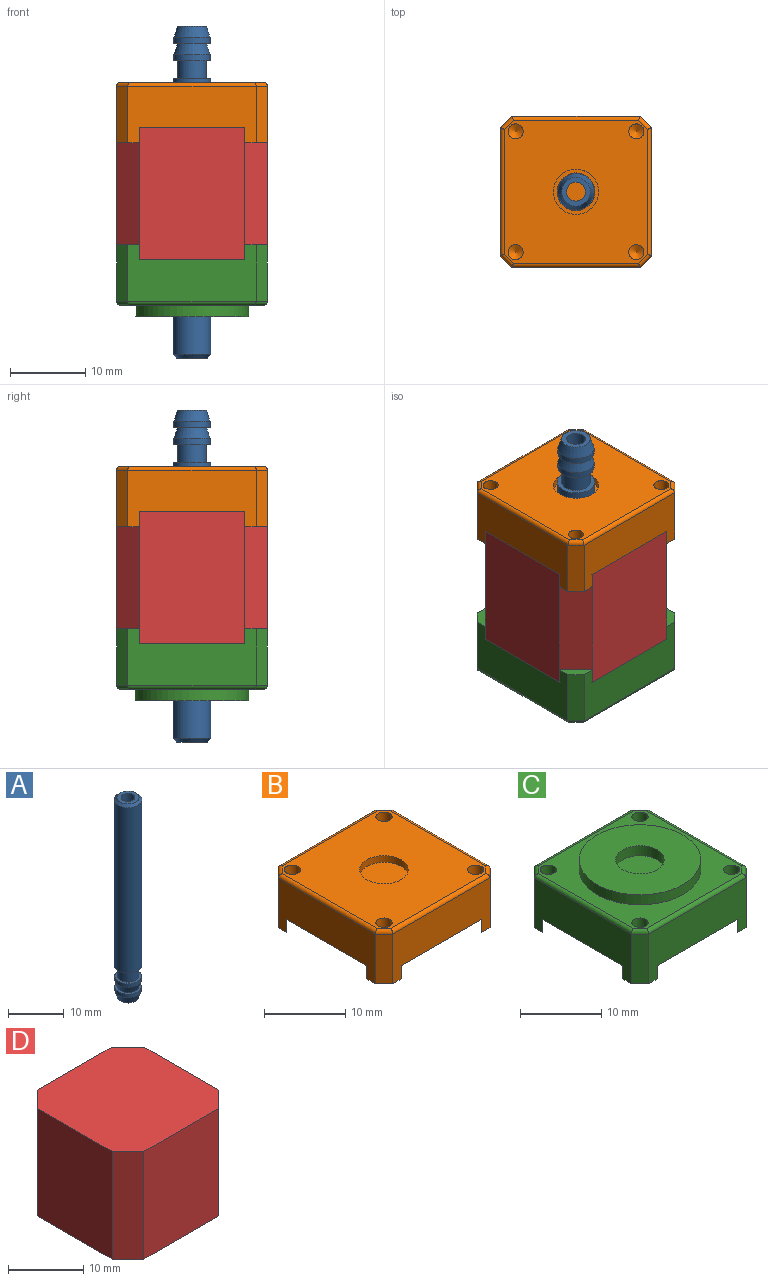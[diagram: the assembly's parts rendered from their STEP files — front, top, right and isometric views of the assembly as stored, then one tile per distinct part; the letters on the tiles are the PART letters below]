
ASSEMBLY  parts=4 mates=3
PART A: 13 faces, bbox 5x5x44 mm
  f0: plane 3.8x3.8mm, normal (0,0,-1), area 6.4mm2, adj f4,f7
  f1: cylinder r=2.5mm len=36.5mm, axis (0,0,-1), area 573.3mm2, adj f3,f6
  f2: plane 4x4mm, normal (0,0,1), area 7.7mm2, adj f3,f4
  f3: cone r=2mm half-angle=45deg, axis (0,0,-1), area 10mm2, adj f1,f2
  f4: cylinder r=1.25mm len=44mm, axis (0,0,1), area 345.6mm2, adj f0,f2
  f5: cylinder r=1.9mm len=3.8mm, axis (0,0,1), area 28.7mm2, adj f6,f12
  f6: plane 5x5mm, normal (0,0,-1), area 8.3mm2, adj f1,f5
  f7: cone r=1.9mm half-angle=18.4deg, axis (0,0,1), area 21.4mm2, adj f0,f8
  f8: cylinder r=2.4mm len=4.8mm, axis (0,0,1), area 12.1mm2, adj f7,f9
  f9: plane 4.8x4.8mm, normal (0,0,1), area 6.8mm2, adj f8,f10
  f10: cone r=1.9mm half-angle=18.4deg, axis (0,0,1), area 21.4mm2, adj f9,f11
  f11: cylinder r=2.4mm len=4.8mm, axis (0,0,1), area 12.1mm2, adj f10,f12
  f12: plane 4.8x4.8mm, normal (0,0,1), area 6.8mm2, adj f5,f11
PART B: 36 faces, bbox 20x20x8 mm
  f0: plane 20x20mm, normal (0,0,-1), area 382mm2, adj f1,f3,f5,f7,f12,f14,f16,f18
  f1: plane 17x7.5mm, normal (0,1,0), area 99.5mm2, adj f0,f2,f8,f14,f15,f18,f19,f30
  f2: plane 7.5x1.5mm, normal (-0.71,0.71,0), area 15.9mm2, adj f1,f3,f19,f32
  f3: plane 17x7.5mm, normal (-1,0,0), area 99.5mm2, adj f0,f2,f4,f16,f17,f18,f19,f34
  f4: plane 7.5x1.5mm, normal (-0.71,-0.71,0), area 15.9mm2, adj f3,f5,f17,f35
  f5: plane 17x7.5mm, normal (0,-1,0), area 99.5mm2, adj f0,f4,f6,f12,f13,f16,f17,f33
  f6: plane 7.5x1.5mm, normal (0.71,-0.71,0), area 15.9mm2, adj f5,f7,f13,f31
  f7: plane 17x7.5mm, normal (1,0,0), area 99.5mm2, adj f0,f6,f8,f12,f13,f14,f15,f29
  f8: plane 7.5x1.5mm, normal (0.71,0.71,0), area 15.9mm2, adj f1,f7,f15,f28
  f9: plane 19x19mm, normal (0,0,1), area 317.2mm2, adj f10,f21,f23,f25,f27,f28,f29,f30
  f10: cylinder r=3mm len=6mm, axis (0,0,1), area 18.8mm2, adj f9,f11
  f11: plane 6x6mm, normal (0,0,1), area 28.3mm2, adj f10
  f12: plane 3x3mm, normal (-0.71,0.71,0), area 8.5mm2, adj f0,f5,f7,f13
  f13: plane 3x3mm, normal (0,0,-1), area 3.4mm2, adj f5,f6,f7,f12
  f14: plane 3x3mm, normal (-0.71,-0.71,0), area 8.5mm2, adj f0,f1,f7,f15
  f15: plane 3x3mm, normal (0,0,-1), area 3.4mm2, adj f1,f7,f8,f14
  f16: plane 3x3mm, normal (0.71,0.71,0), area 8.5mm2, adj f0,f3,f5,f17
  f17: plane 3x3mm, normal (0,0,-1), area 3.4mm2, adj f3,f4,f5,f16
  f18: plane 3x3mm, normal (0.71,-0.71,0), area 8.5mm2, adj f0,f1,f3,f19
  f19: plane 3x3mm, normal (0,0,-1), area 3.4mm2, adj f1,f2,f3,f18
  f20: cone r=0mm half-angle=59deg, axis (0,0,1), area 3.7mm2, adj f21
  f21: cylinder r=1mm len=3mm, axis (0,0,1), area 18.8mm2, adj f9,f20
  f22: cone r=0mm half-angle=59deg, axis (0,0,1), area 3.7mm2, adj f23
  f23: cylinder r=1mm len=3mm, axis (0,0,1), area 18.8mm2, adj f9,f22
  f24: cone r=0mm half-angle=59deg, axis (0,0,1), area 3.7mm2, adj f25
  f25: cylinder r=1mm len=3mm, axis (0,0,1), area 18.8mm2, adj f9,f24
  f26: cone r=0mm half-angle=59deg, axis (0,0,1), area 3.7mm2, adj f27
  f27: cylinder r=1mm len=3mm, axis (0,0,1), area 18.8mm2, adj f9,f26
  f28: cylinder r=0.5mm len=1.85mm, axis (-0.71,0.71,0), area 1.5mm2, adj f8,f9,f29,f30
  f29: cylinder r=0.5mm len=17mm, axis (0,1,0), area 13.2mm2, adj f7,f9,f28,f31
  f30: cylinder r=0.5mm len=17mm, axis (-1,0,0), area 13.2mm2, adj f1,f9,f28,f32
  f31: cylinder r=0.5mm len=1.85mm, axis (0.71,0.71,0), area 1.5mm2, adj f6,f9,f29,f33
  f32: cylinder r=0.5mm len=1.85mm, axis (-0.71,-0.71,0), area 1.5mm2, adj f2,f9,f30,f34
  f33: cylinder r=0.5mm len=17mm, axis (1,0,0), area 13.2mm2, adj f5,f9,f31,f35
  f34: cylinder r=0.5mm len=17mm, axis (0,-1,0), area 13.2mm2, adj f3,f9,f32,f35
  f35: cylinder r=0.5mm len=1.85mm, axis (0.71,-0.71,0), area 1.5mm2, adj f4,f9,f33,f34
PART C: 38 faces, bbox 20x20x9.5 mm
  f0: plane 20x20mm, normal (0,0,-1), area 382mm2, adj f1,f3,f5,f7,f14,f16,f18,f20
  f1: plane 17x7.5mm, normal (0,-1,0), area 99.5mm2, adj f0,f2,f8,f16,f17,f20,f21,f37
  f2: plane 7.5x1.5mm, normal (0.71,-0.71,0), area 15.9mm2, adj f1,f3,f17,f35
  f3: plane 17x7.5mm, normal (1,0,0), area 99.5mm2, adj f0,f2,f4,f14,f15,f16,f17,f33
  f4: plane 7.5x1.5mm, normal (0.71,0.71,0), area 15.9mm2, adj f3,f5,f15,f31
  f5: plane 17x7.5mm, normal (0,1,0), area 99.5mm2, adj f0,f4,f6,f14,f15,f18,f19,f30
  f6: plane 7.5x1.5mm, normal (-0.71,0.71,0), area 15.9mm2, adj f5,f7,f19,f32
  f7: plane 17x7.5mm, normal (-1,0,0), area 99.5mm2, adj f0,f6,f8,f18,f19,f20,f21,f34
  f8: plane 7.5x1.5mm, normal (-0.71,-0.71,0), area 15.9mm2, adj f1,f7,f21,f36
  f9: plane 19x19mm, normal (0,0,1), area 168.8mm2, adj f11,f23,f25,f27,f29,f30,f31,f32
  f10: cylinder r=3mm len=6mm, axis (0,0,-1), area 28.3mm2, adj f12,f13
  f11: cylinder r=7.5mm len=15mm, axis (0,0,-1), area 70.7mm2, adj f9,f12
  f12: plane 15x15mm, normal (0,0,1), area 148.4mm2, adj f10,f11
  f13: plane 6x6mm, normal (0,0,1), area 28.3mm2, adj f10
  f14: plane 3x3mm, normal (-0.71,-0.71,0), area 8.5mm2, adj f0,f3,f5,f15
  f15: plane 3x3mm, normal (0,0,-1), area 3.4mm2, adj f3,f4,f5,f14
  f16: plane 3x3mm, normal (-0.71,0.71,0), area 8.5mm2, adj f0,f1,f3,f17
  f17: plane 3x3mm, normal (0,0,-1), area 3.4mm2, adj f1,f2,f3,f16
  f18: plane 3x3mm, normal (0.71,-0.71,0), area 8.5mm2, adj f0,f5,f7,f19
  f19: plane 3x3mm, normal (0,0,-1), area 3.4mm2, adj f5,f6,f7,f18
  f20: plane 3x3mm, normal (0.71,0.71,0), area 8.5mm2, adj f0,f1,f7,f21
  f21: plane 3x3mm, normal (0,0,-1), area 3.4mm2, adj f1,f7,f8,f20
  f22: cone r=0mm half-angle=59deg, axis (0,0,1), area 3.7mm2, adj f23
  f23: cylinder r=1mm len=3mm, axis (0,0,1), area 18.8mm2, adj f9,f22
  f24: cone r=0mm half-angle=59deg, axis (0,0,1), area 3.7mm2, adj f25
  f25: cylinder r=1mm len=3mm, axis (0,0,1), area 18.8mm2, adj f9,f24
  f26: cone r=0mm half-angle=59deg, axis (0,0,1), area 3.7mm2, adj f27
  f27: cylinder r=1mm len=3mm, axis (0,0,1), area 18.8mm2, adj f9,f26
  f28: cone r=0mm half-angle=59deg, axis (0,0,1), area 3.7mm2, adj f29
  f29: cylinder r=1mm len=3mm, axis (0,0,1), area 18.8mm2, adj f9,f28
  f30: cylinder r=0.5mm len=17mm, axis (-1,0,0), area 13.2mm2, adj f5,f9,f31,f32
  f31: cylinder r=0.5mm len=1.85mm, axis (-0.71,0.71,0), area 1.5mm2, adj f4,f9,f30,f33
  f32: cylinder r=0.5mm len=1.85mm, axis (-0.71,-0.71,0), area 1.5mm2, adj f6,f9,f30,f34
  f33: cylinder r=0.5mm len=17mm, axis (0,1,0), area 13.2mm2, adj f3,f9,f31,f35
  f34: cylinder r=0.5mm len=17mm, axis (0,-1,0), area 13.2mm2, adj f7,f9,f32,f36
  f35: cylinder r=0.5mm len=1.85mm, axis (0.71,0.71,0), area 1.5mm2, adj f2,f9,f33,f37
  f36: cylinder r=0.5mm len=1.85mm, axis (0.71,-0.71,0), area 1.5mm2, adj f8,f9,f34,f37
  f37: cylinder r=0.5mm len=17mm, axis (1,0,0), area 13.2mm2, adj f1,f9,f35,f36
PART D: 10 faces, bbox 20x20x17.5 mm
  f0: plane 17.5x14mm, normal (0,1,0), area 245mm2, adj f1,f7,f8,f9
  f1: plane 17.5x3mm, normal (-0.71,0.71,0), area 74.2mm2, adj f0,f2,f8,f9
  f2: plane 17.5x14mm, normal (-1,0,0), area 245mm2, adj f1,f3,f8,f9
  f3: plane 17.5x3mm, normal (-0.71,-0.71,0), area 74.2mm2, adj f2,f4,f8,f9
  f4: plane 17.5x14mm, normal (0,-1,0), area 245mm2, adj f3,f5,f8,f9
  f5: plane 17.5x3mm, normal (0.71,-0.71,0), area 74.2mm2, adj f4,f6,f8,f9
  f6: plane 17.5x14mm, normal (1,0,0), area 245mm2, adj f5,f7,f8,f9
  f7: plane 17.5x3mm, normal (0.71,0.71,0), area 74.2mm2, adj f0,f6,f8,f9
  f8: plane 20x20mm, normal (0,0,1), area 382mm2, adj f0,f1,f2,f3,f4,f5,f6,f7
  f9: plane 20x20mm, normal (0,0,-1), area 382mm2, adj f0,f1,f2,f3,f4,f5,f6,f7
PLACE A rot(axis=(0.2,-0.98,0),180deg) t=(-56.49,42.88,-25)mm
PLACE B t=(8.83,5.93,4.5)mm
PLACE C rot(axis=(1,0,0),180deg) t=(-41.17,5.93,-25)mm
PLACE D rot(axis=(1,0,0),180deg) t=(-81.17,5.93,-1.5)mm
MATE revolute A.f1 <-> C.f10  axis (0,0,1) through (-41.17,5.93,-25)mm
MATE fastened D.f8 <-> C.f10  axis (0,0,-1) through (-41.17,5.93,-19)mm
MATE fastened D.f9 <-> B.f10  axis (0,0,1) through (-41.17,5.93,-1.5)mm
